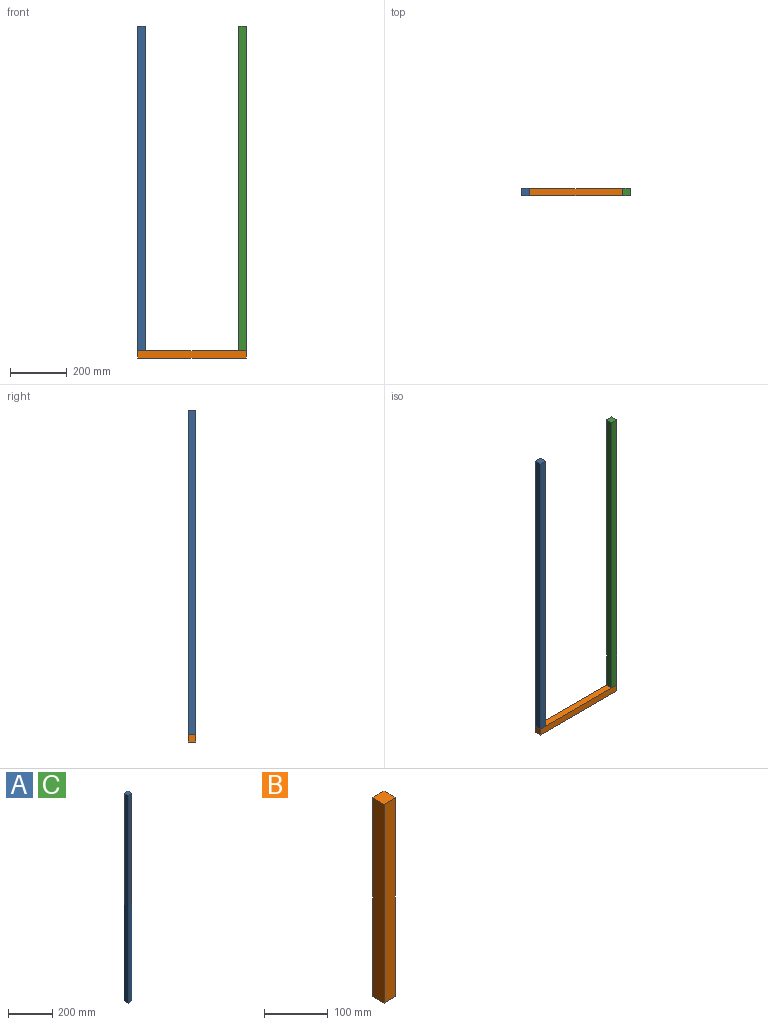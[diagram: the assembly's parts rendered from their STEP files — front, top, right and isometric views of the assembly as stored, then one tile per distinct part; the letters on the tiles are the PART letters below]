
ASSEMBLY  parts=3 mates=2
PART A: 6 faces, bbox 25.4x25.4x1143 mm
  f0: plane 1143x25.4mm, normal (0,1,0), area 29032.2mm2, adj f1,f3,f4,f5
  f1: plane 1143x25.4mm, normal (-1,0,0), area 29032.2mm2, adj f0,f2,f4,f5
  f2: plane 1143x25.4mm, normal (0,-1,0), area 29032.2mm2, adj f1,f3,f4,f5
  f3: plane 1143x25.4mm, normal (1,0,0), area 29032.2mm2, adj f0,f2,f4,f5
  f4: plane 25.4x25.4mm, normal (0,0,1), area 645.2mm2, adj f0,f1,f2,f3
  f5: plane 25.4x25.4mm, normal (0,0,-1), area 645.2mm2, adj f0,f1,f2,f3
PART B: 6 faces, bbox 25.4x25.4x381 mm
  f0: plane 381x25.4mm, normal (0,1,0), area 9677.4mm2, adj f1,f3,f4,f5
  f1: plane 381x25.4mm, normal (-1,0,0), area 9677.4mm2, adj f0,f2,f4,f5
  f2: plane 381x25.4mm, normal (0,-1,0), area 9677.4mm2, adj f1,f3,f4,f5
  f3: plane 381x25.4mm, normal (1,0,0), area 9677.4mm2, adj f0,f2,f4,f5
  f4: plane 25.4x25.4mm, normal (0,0,1), area 645.2mm2, adj f0,f1,f2,f3
  f5: plane 25.4x25.4mm, normal (0,0,-1), area 645.2mm2, adj f0,f1,f2,f3
PART C: same geometry as A
PLACE A t=(-103.79,70.23,16.01)mm
PLACE B rot(axis=(0,-1,0),90deg) t=(224.26,70.12,-30.32)mm
PLACE C t=(251.81,70.23,16.01)mm
MATE parallel C.f3 <-> A.f1  axis (1,0,0) through (224.26,111.99,587.51)mm
MATE parallel B.f3 <-> A.f5  axis (0,0,1) through (-156.74,111.99,16.01)mm
